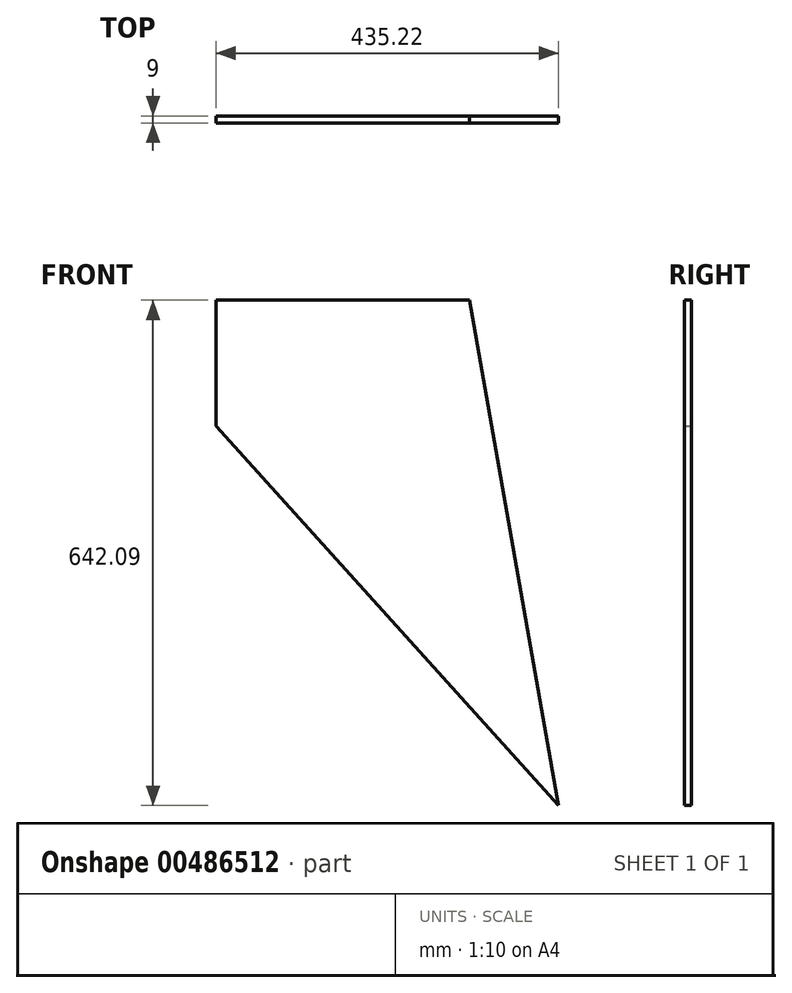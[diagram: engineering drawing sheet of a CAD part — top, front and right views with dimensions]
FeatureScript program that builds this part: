
annotation { "Feature Type Name" : "Feature", "Feature Type Description" : "" }
export const myFeature = defineFeature(function(context is Context, id is Id, definition is map)
    precondition{}
    {
        {
            var Q0;
            Q0=qCreatedBy(makeId("Front.planeOp"),FACE);
            var sketch = newSketch(context, id + "F0", { "sketchPlane" : qUnion([Q0])});
            skLineSegment(sketch, "E0", {"start": v(-113.22, 642.1) * mm, "end": v(-435.22, 642.1) * mm});
            skLineSegment(sketch, "E1", {"start": v(-435.22, 642.1) * mm, "end": v(-435.22, 482.1) * mm});
            skLineSegment(sketch, "E2", {"start": v(-435.22, 482.1) * mm, "end": v(0, 0) * mm});
            skLineSegment(sketch, "E3", {"start": v(0, 0) * mm, "end": v(-113.22, 642.1) * mm});
            skSolve(sketch);
        }
        {
            var Q0;
            Q0=makeQuery(id+"F0.imprint","IMPRINT",FACE,{"disambiguationData":[TD([[makeQuery(id+"F0.imprint","IMPRINT",EDGE,{"derivedFrom":sQuery(id+"F0.wireOp",EDGE,"E0")}),1.0]])]});
            extrude(context, id + "F1", {"entities" : qUnion([Q0]), "depth" : 9 * mm, "offsetDistance" : 25 * mm});
        }
    });
